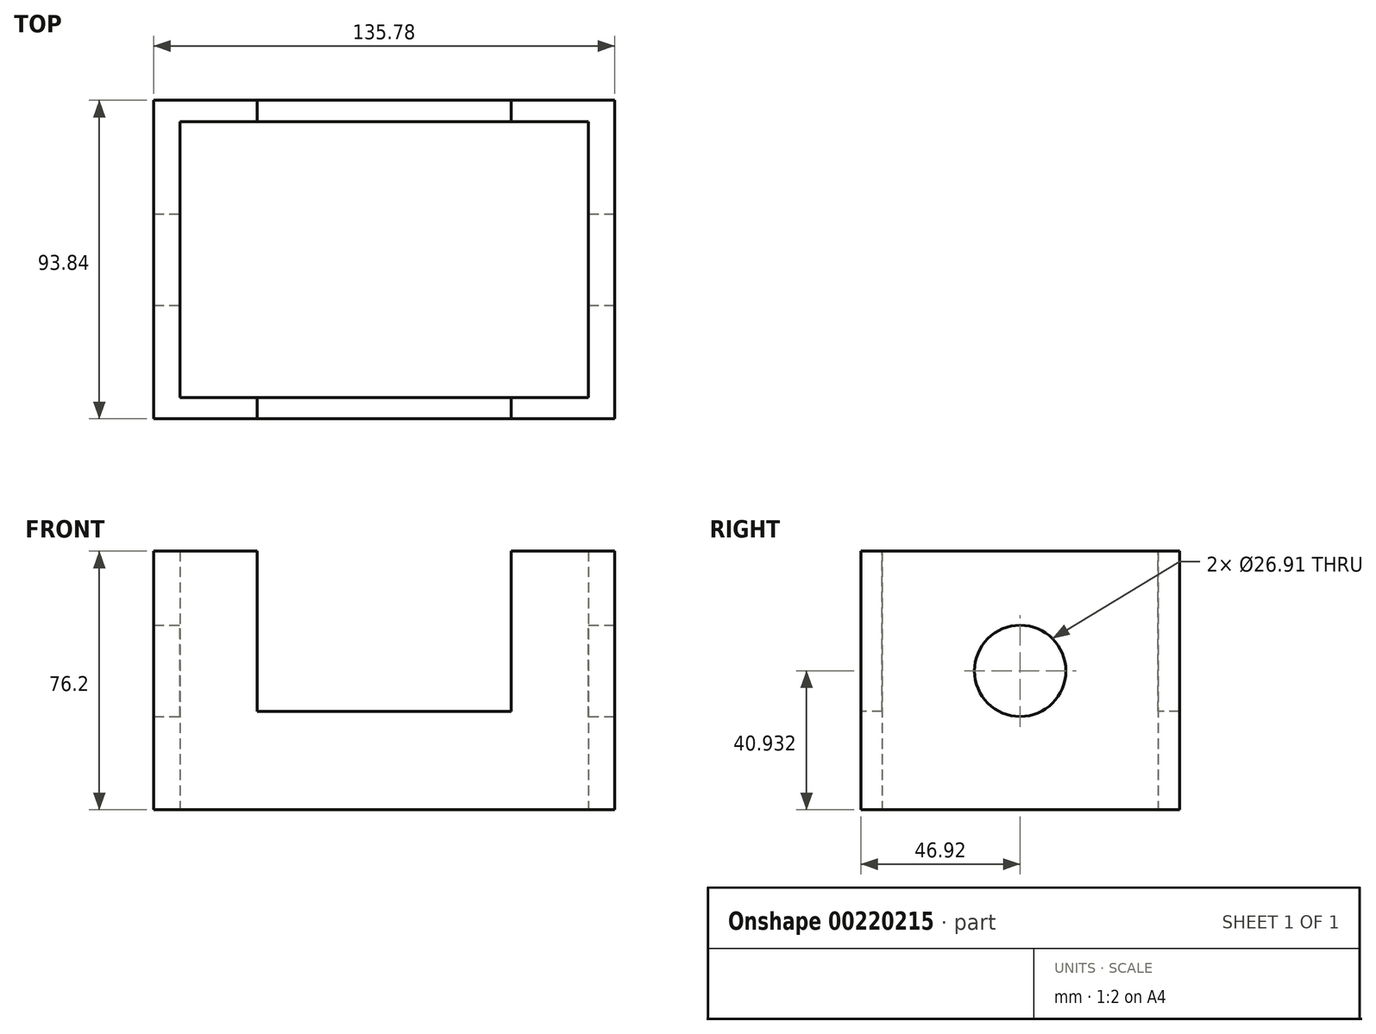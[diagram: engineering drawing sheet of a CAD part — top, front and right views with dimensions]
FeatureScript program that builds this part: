
annotation { "Feature Type Name" : "Feature", "Feature Type Description" : "" }
export const myFeature = defineFeature(function(context is Context, id is Id, definition is map)
    precondition{}
    {
        {
            var Q0;
            Q0=qCreatedBy(makeId("Top.planeOp"),FACE);
            var sketch = newSketch(context, id + "F0", { "sketchPlane" : qUnion([Q0])});
            skLineSegment(sketch, "E0.bottom", {"start": v(-67.89, 46.92) * mm, "end": v(67.89, 46.92) * mm});
            skLineSegment(sketch, "E0.top", {"start": v(-67.89, -46.92) * mm, "end": v(67.89, -46.92) * mm});
            skLineSegment(sketch, "E0.left", {"start": v(-67.89, 46.92) * mm, "end": v(-67.89, -46.92) * mm});
            skLineSegment(sketch, "E0.right", {"start": v(67.89, 46.92) * mm, "end": v(67.89, -46.92) * mm});
            skPoint(sketch, "E0.middle", {"position": v(0, 0) * mm});
            skLineSegment(sketch, "E1.bottom", {"start": v(-60.19, 40.65) * mm, "end": v(60.19, 40.65) * mm});
            skLineSegment(sketch, "E1.top", {"start": v(-60.19, -40.65) * mm, "end": v(60.19, -40.65) * mm});
            skLineSegment(sketch, "E1.left", {"start": v(-60.19, 40.65) * mm, "end": v(-60.19, -40.65) * mm});
            skLineSegment(sketch, "E1.right", {"start": v(60.19, 40.65) * mm, "end": v(60.19, -40.65) * mm});
            skSolve(sketch);
        }
        {
            var Q0;
            Q0=makeQuery(id+"F0.imprint","IMPRINT",FACE,{"disambiguationData":[TD([[makeQuery(id+"F0.imprint","IMPRINT",EDGE,{"derivedFrom":sQuery(id+"F0.wireOp",EDGE,"E0.bottom")}),-1.0]])]});
            extrude(context, id + "F1", {"entities" : qUnion([Q0]), "depth" : 76.2 * mm});
        }
        {
            var Q0;
            Q0=makeQuery(id+"F1.opExtrude","SWEPT_FACE",FACE,{"disambiguationData":[OSD([sQuery(id+"F0.wireOp",EDGE,"E0.right")])]});
            var sketch = newSketch(context, id + "F2", { "sketchPlane" : qUnion([Q0])});
            skCircle(sketch, "E2", {"center": v(0, 40.93) * mm, "radius": 13.45 * mm});
            skSolve(sketch);
        }
        {
            var Q0;
            Q0 = qSketchRegion(id + "F2", true);
            extrude(context, id + "F3", {"entities" : qUnion([Q0]), "operationType" : NewBodyOperationType.REMOVE, "endBound" : BoundingType.THROUGH_ALL, "oppositeDirection" : true, "depth" : 25.4 * mm});
        }
        {
            var Q0;
            Q0=makeQuery(id+"F1.opExtrude","SWEPT_FACE",FACE,{"disambiguationData":[OSD([sQuery(id+"F0.wireOp",EDGE,"E0.top")])]});
            var sketch = newSketch(context, id + "F4", { "sketchPlane" : qUnion([Q0])});
            skLineSegment(sketch, "E3.bottom", {"start": v(37.37, 76.2) * mm, "end": v(-37.37, 76.2) * mm});
            skLineSegment(sketch, "E3.top", {"start": v(37.37, 29.05) * mm, "end": v(-37.37, 29.05) * mm});
            skLineSegment(sketch, "E3.left", {"start": v(37.37, 76.2) * mm, "end": v(37.37, 29.05) * mm});
            skLineSegment(sketch, "E3.right", {"start": v(-37.37, 76.2) * mm, "end": v(-37.37, 29.05) * mm});
            skPoint(sketch, "E3.middle", {"position": v(0, 52.63) * mm});
            skSolve(sketch);
        }
        {
            var Q0;
            Q0=makeQuery(id+"F4.imprint","IMPRINT",FACE,{"disambiguationData":[TD([[makeQuery(id+"F4.imprint","IMPRINT",EDGE,{"derivedFrom":sQuery(id+"F4.wireOp",EDGE,"E3.bottom")}),-1.0]])]});
            extrude(context, id + "F5", {"entities" : qUnion([Q0]), "operationType" : NewBodyOperationType.REMOVE, "endBound" : BoundingType.THROUGH_ALL, "oppositeDirection" : true, "depth" : 25.4 * mm});
        }
    });
